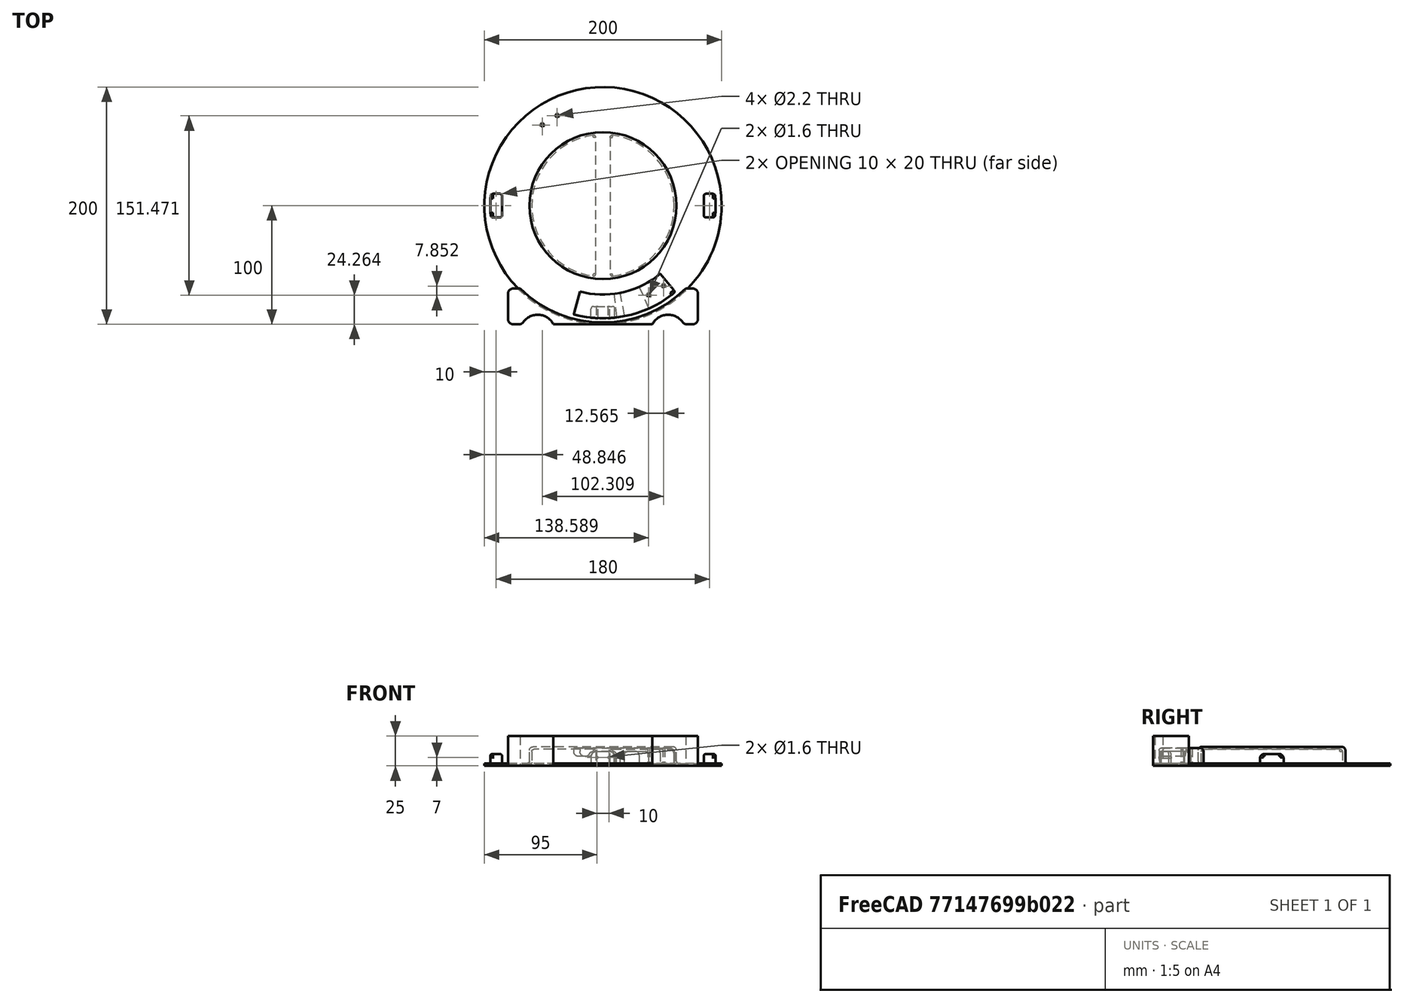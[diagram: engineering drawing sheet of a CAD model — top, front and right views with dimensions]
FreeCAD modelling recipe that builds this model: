
FCSTD DOCUMENT  (FreeCAD 1.0R39109 (Git))
Label: CarToolBox
License: All rights reserved
LicenseURL: https://en.wikipedia.org/wiki/All_rights_reserved
objects: Part::Cylinder×20, Part::Fillet×15, Part::MultiFuse×10, Part::Cut×9, Part::Box×4, Part::Chamfer×2, Part::Feature×2, Part::MultiCommon×1, Part::FeaturePython×1
note: 64 computed .brp shape members not serialized (recipe doc carries the construction recipe); baked Part::Feature solids carry a one-line shape summary decoded from their .brp

FEATURE [Part::Box] Box002  label="Cube001"
  AttacherType = Attacher::AttachEngine3D
  Height = 10
  Length = 20
  Placement = pos=(-10,-95,0) rot=(0,0,1;0rad)
  Width = 10
FEATURE [Part::Cylinder] Cylinder009
  Angle = 360
  AttacherType = Attacher::AttachEngine3D
  FirstAngle = 0
  Height = 10
  Radius = 95
  SecondAngle = 0
FEATURE [Part::MultiCommon] Common
  Shapes = -> [Cylinder009,Box002]
FEATURE [Part::Fillet] Fillet006
  Base = -> Common
  EdgeLinks = -> Common [Edge11,Edge13]
  Edges = 2 edges r=4: [Edge11,Edge13]
FEATURE [Part::Fillet] Fillet007
  Base = -> Fillet006
  EdgeLinks = -> Fillet006 [Edge6]
  Edges = 1 edges r=2: [Edge6]
FEATURE [Part::Cylinder] Cylinder010  label="Screw003"
  Angle = 360
  AttacherType = Attacher::AttachEngine3D
  FirstAngle = 0
  Height = 20
  Placement = pos=(-5,-100,5) rot=(-1,0,0;1.5708rad)
  Radius = 0.8
  SecondAngle = 0
FEATURE [Part::Cylinder] Cylinder011  label="Screw004"
  Angle = 360
  AttacherType = Attacher::AttachEngine3D
  FirstAngle = 0
  Height = 20
  Placement = pos=(5,-100,5) rot=(-1,0,0;1.5708rad)
  Radius = 0.8
  SecondAngle = 0
FEATURE [Part::MultiFuse] Fusion005
  Shapes = -> [Cylinder010,Cylinder011]
FEATURE [Part::Cut] Cut002  label="CloseTooth"
  Base = -> Fillet007
  Placement = pos=(0,0,2) rot=(0,0,1;0rad)
  Tool = -> Fusion005
FEATURE [Part::Cylinder] Cylinder014  label="MainTooth"
  Angle = 55
  AttacherType = Attacher::AttachEngine3D
  FirstAngle = 0
  Height = 13
  Placement = pos=(0,0,2) rot=(0,0,1;-1.8326rad)
  Radius = 95
  SecondAngle = 0
FEATURE [Part::Cylinder] Cylinder015
  Angle = 14
  AttacherType = Attacher::AttachEngine3D
  FirstAngle = 0
  Height = 10
  Placement = pos=(0,0,2) rot=(0,0,1;-1.69297rad)
  Radius = 95
  SecondAngle = 0
FEATURE [Part::Cylinder] Cylinder016
  Angle = 140
  AttacherType = Attacher::AttachEngine3D
  FirstAngle = 0
  Height = 19
  Placement = pos=(0,0,2) rot=(0,0,1;-1.91986rad)
  Radius = 75
  SecondAngle = 0
FEATURE [Part::Cut] Cut
  Base = -> Cylinder014
  Tool = -> Cylinder016
FEATURE [Part::Fillet] Fillet013
  Base = -> Cut
  EdgeLinks = -> Cut [Edge6]
  Edges = 1 edges r=4: [Edge6]
FEATURE [Part::Fillet] Fillet014
  Base = -> Fillet013
  EdgeLinks = -> Fillet013 [Edge4]
  Edges = 1 edges r=2: [Edge4]
FEATURE [Part::Box] Box  label="Cube"
  AttacherType = Attacher::AttachEngine3D
  Height = 8
  Length = 30
  Placement = pos=(-35,-100,0) rot=(0,0,1;0rad)
  Width = 30
FEATURE [Part::Cylinder] Cylinder017
  Angle = 360
  AttacherType = Attacher::AttachEngine3D
  FirstAngle = 0
  Height = 20
  Placement = pos=(85,0,0) rot=(0,0,1;0rad)
  Radius = 0.8
  SecondAngle = 0
FEATURE [Part::Cylinder] Cylinder018
  Angle = 360
  AttacherType = Attacher::AttachEngine3D
  FirstAngle = 0
  Height = 20
  Placement = pos=(-85,0,0) rot=(0,0,1;0rad)
  Radius = 0.8
  SecondAngle = 0
FEATURE [Part::Cylinder] Cylinder027
  Angle = 360
  AttacherType = Attacher::AttachEngine3D
  FirstAngle = 0
  Height = 16
  Radius = 100
  SecondAngle = 0
FEATURE [Part::Cylinder] Cylinder028
  Angle = 360
  AttacherType = Attacher::AttachEngine3D
  FirstAngle = 0
  Height = 14
  Radius = 60
  SecondAngle = 0
FEATURE [Part::Fillet] Fillet020
  Base = -> Cylinder028
  EdgeLinks = -> Cylinder028 [Edge3]
  Edges = 1 edges r=2: [Edge3]
FEATURE [Part::Box] Box007  label="Cube006"
  AttacherType = Attacher::AttachEngine3D
  Height = 15
  Length = 12
  Placement = pos=(-6,-100,0) rot=(0,0,1;0rad)
  Width = 200
FEATURE [Part::FeaturePython] Tube  # WARN: FeaturePython — macro-defined, semantics opaque (R4)
  AttacherType = Attacher::AttachEngine3D
  Height = 17
  InnerRadius = 62
  OuterRadius = 100
  Placement = pos=(0,0,2) rot=(0,0,1;0rad)
FEATURE [Part::Fillet] Fillet022
  Base = -> Tube
  EdgeLinks = -> Tube [Edge5]
  Edges = 1 edges r=2: [Edge5]
FEATURE [Part::Cut] Cut014
  Base = -> Cylinder027
  Tool = -> Fillet022
FEATURE [Part::Cut] Cut015
  Base = -> Fillet020
  Tool = -> Box007
FEATURE [Part::Fillet] Fillet023
  Base = -> Cut015
  EdgeLinks = -> Cut015 [Edge8,Edge20]
  Edges = 2 edges r=2: [Edge8,Edge20]
FEATURE [Part::Fillet] Fillet024
  Base = -> Cut014
  EdgeLinks = -> Cut014 [Edge8]
  Edges = 1 edges r=3: [Edge8]
FEATURE [Part::Cut] Cut016
  Base = -> Fillet024
  Tool = -> Fillet023
FEATURE [Part::Fillet] Fillet025  label="1_Cover"
  Base = -> Cut016
  EdgeLinks = -> Cut016 [Edge11,Edge15]
  Edges = 2 edges r=3: [Edge11,Edge15]
FEATURE [Part::Cylinder] Cylinder021
  Angle = 360
  AttacherType = Attacher::AttachEngine3D
  FirstAngle = 0
  Height = 20
  Placement = pos=(85,0,0) rot=(0,0,1;0rad)
  Radius = 1.1
  SecondAngle = 0
FEATURE [Part::Cylinder] Cylinder024
  Angle = 360
  AttacherType = Attacher::AttachEngine3D
  FirstAngle = 0
  Height = 20
  Placement = pos=(-85,0,0) rot=(0,0,1;0rad)
  Radius = 1.1
  SecondAngle = 0
FEATURE [Part::Cylinder] Cylinder023
  Angle = 360
  AttacherType = Attacher::AttachEngine3D
  FirstAngle = 0
  Height = 20
  Placement = pos=(85,0,0) rot=(0,0,1;0rad)
  Radius = 1.1
  SecondAngle = 0
FEATURE [Part::MultiFuse] Fusion010
  Placement = pos=(0,0,0) rot=(0,0,1;0.174533rad)
  Shapes = -> [Cylinder024,Cylinder023]
FEATURE [Part::Cylinder] Cylinder022
  Angle = 360
  AttacherType = Attacher::AttachEngine3D
  FirstAngle = 0
  Height = 20
  Placement = pos=(-85,0,0) rot=(0,0,1;0rad)
  Radius = 1.1
  SecondAngle = 0
FEATURE [Part::MultiFuse] Fusion009
  Shapes = -> [Cylinder022,Cylinder021]
FEATURE [Part::MultiFuse] Fusion011  label="4_ToothScrewHolles001"
  Placement = pos=(0,0,0) rot=(0,0,1;-1.09956rad)
  Shapes = -> [Fusion010,Fusion009]
FEATURE [Part::Cut] Cut017
  Base = -> Fillet025
  Tool = -> Fusion011
FEATURE [Part::Chamfer] Chamfer001
  Base = -> Cut017
  EdgeLinks = -> Cut017 [Edge8,Edge9,Edge2,Edge3]
  Edges = 4 edges r=1: [Edge8,Edge9,Edge2,Edge3]
FEATURE [Part::MultiFuse] Fusion006
  Shapes = -> [Cylinder018,Cylinder017]
FEATURE [Part::Cylinder] Cylinder019
  Angle = 360
  AttacherType = Attacher::AttachEngine3D
  FirstAngle = 0
  Height = 20
  Placement = pos=(85,0,0) rot=(0,0,1;0rad)
  Radius = 0.8
  SecondAngle = 0
FEATURE [Part::Cylinder] Cylinder020
  Angle = 360
  AttacherType = Attacher::AttachEngine3D
  FirstAngle = 0
  Height = 20
  Placement = pos=(-85,0,0) rot=(0,0,1;0rad)
  Radius = 0.8
  SecondAngle = 0
FEATURE [Part::MultiFuse] Fusion007
  Placement = pos=(0,0,0) rot=(0,0,1;0.174533rad)
  Shapes = -> [Cylinder020,Cylinder019]
FEATURE [Part::MultiFuse] Fusion008  label="ToothScrewHolles"
  Placement = pos=(0,0,0) rot=(0,0,1;-1.09956rad)
  Shapes = -> [Fusion007,Fusion006]
FEATURE [Part::Cylinder] Cylinder029
  Angle = 13
  AttacherType = Attacher::AttachEngine3D
  FirstAngle = 0
  Height = 10
  Placement = pos=(0,0,2) rot=(0,0,1;-1.37881rad)
  Radius = 95
  SecondAngle = 0
FEATURE [Part::Fillet] Fillet026
  Base = -> Cylinder029
  EdgeLinks = -> Cylinder029 [Edge7,Edge9]
  Edges = 2 edges r=3: [Edge7,Edge9]
FEATURE [Part::Fillet] Fillet
  Base = -> Cylinder015
  EdgeLinks = -> Cylinder015 [Edge7,Edge9]
  Edges = 2 edges r=3: [Edge7,Edge9]
FEATURE [Part::MultiFuse] Fusion
  Shapes = -> [Fillet026,Fillet,Box]
FEATURE [Part::Cut] Cut018
  Base = -> Fillet014
  Tool = -> Fusion
FEATURE [Part::Fillet] Fillet027
  Base = -> Cut018
  EdgeLinks = -> Cut018 [Edge18,Edge19]
  Edges = 2 edges r=4: [Edge18,Edge19]
FEATURE [Part::Cut] Cut019
  Base = -> Fillet027
  Tool = -> Fusion008
FEATURE [Part::Chamfer] Chamfer  label="CloseArm"
  Base = -> Cut019
  EdgeLinks = -> Cut019 [Edge48,Edge49]
  Edges = 2 edges r=1: [Edge48,Edge49]
FEATURE [Part::Feature] Fillet030
  Placement = pos=(0,0,0) rot=(0,0,1;1.5708rad)
  shape: bbox 10 x 20.66 x 10.33 mm, 14 faces (baked)
FEATURE [Part::Feature] Fillet031
  Placement = pos=(0,0,0) rot=(0,0,1;-1.5708rad)
  shape: bbox 10 x 20.66 x 10.33 mm, 14 faces (baked)
FEATURE [Part::Fillet] Fillet032
  Base = -> Fillet030
  EdgeLinks = -> Fillet030 [Edge3]
  Edges = 1 edges r=2: [Edge3]
FEATURE [Part::Fillet] Fillet033
  Base = -> Fillet031
  EdgeLinks = -> Fillet031 [Edge3]
  Edges = 1 edges r=2: [Edge3]
FEATURE [Part::MultiFuse] Fusion012  label="Cap"
  Shapes = -> [Fillet033,Fillet032,Chamfer001]
FEATURE [Part::Cylinder] Cylinder030
  Angle = 360
  AttacherType = Attacher::AttachEngine3D
  FirstAngle = 0
  Height = 25
  Placement = pos=(0,1.5,0) rot=(0,0,1;0rad)
  Radius = 100
  SecondAngle = 0
FEATURE [Part::Box] Box008  label="Cube007"
  AttacherType = Attacher::AttachEngine3D
  Height = 25
  Length = 160
  Placement = pos=(-80,-100,0) rot=(0,0,1;0rad)
  Width = 30
FEATURE [Part::Cylinder] Cylinder031
  Angle = 360
  AttacherType = Attacher::AttachEngine3D
  FirstAngle = 0
  Height = 25
  Placement = pos=(-55,-107,0) rot=(0,0,1;0rad)
  Radius = 15
  SecondAngle = 0
FEATURE [Part::Cylinder] Cylinder032
  Angle = 360
  AttacherType = Attacher::AttachEngine3D
  FirstAngle = 0
  Height = 25
  Placement = pos=(55,-107,0) rot=(0,0,1;0rad)
  Radius = 15
  SecondAngle = 0
FEATURE [Part::MultiFuse] Fusion013
  Shapes = -> [Cylinder031,Cylinder032,Cylinder030]
FEATURE [Part::Cut] Cut020
  Base = -> Box008
  Tool = -> Fusion013
FEATURE [Part::Fillet] Fillet034  label="Holder"
  Base = -> Cut020
  EdgeLinks = -> Cut020 [Edge1,Edge3,Edge6,Edge27,Edge28,Edge29]
  Edges = 6 edges r=4: [Edge1,Edge3,Edge6,Edge27,Edge28,Edge29]
